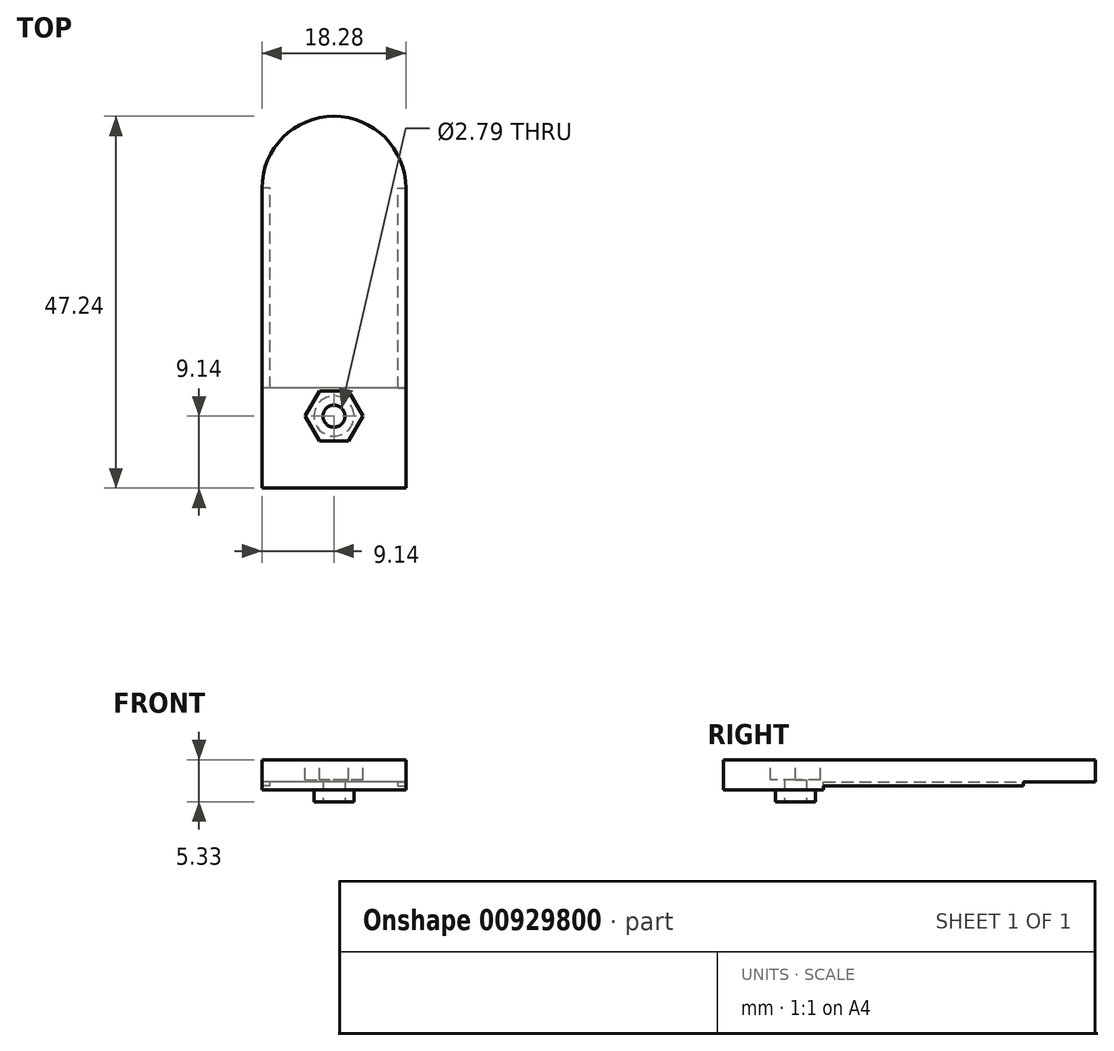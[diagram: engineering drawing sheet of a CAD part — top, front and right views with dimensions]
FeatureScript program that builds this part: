
annotation { "Feature Type Name" : "Feature", "Feature Type Description" : "" }
export const myFeature = defineFeature(function(context is Context, id is Id, definition is map)
    precondition{}
    {
        {
            var Q0;
            Q0=qCreatedBy(makeId("Top.planeOp"),FACE);
            var sketch = newSketch(context, id + "F0", { "sketchPlane" : qUnion([Q0])});
            skCircle(sketch, "E0", {"center": v(0, 0) * mm, "radius": 2.54 * mm});
            skLineSegment(sketch, "E1", {"start": v(0, 0) * mm, "end": v(-8.13, 0) * mm});
            skLineSegment(sketch, "E2", {"start": v(0, 0) * mm, "end": v(8.13, 0) * mm});
            skLineSegment(sketch, "E3", {"start": v(-2.54, 0) * mm, "end": v(-8.13, 0) * mm});
            skLineSegment(sketch, "E4", {"start": v(0, -2.54) * mm, "end": v(0, -9.14) * mm});
            skLineSegment(sketch, "E5", {"start": v(-8.13, 0) * mm, "end": v(-9.14, 0) * mm});
            skLineSegment(sketch, "E6", {"start": v(8.13, 0) * mm, "end": v(9.14, 0) * mm});
            skLineSegment(sketch, "E7", {"start": v(9.14, 0) * mm, "end": v(9.14, -9.14) * mm});
            skLineSegment(sketch, "E8.bottom", {"start": v(9.14, -9.14) * mm, "end": v(-9.14, -9.14) * mm});
            skLineSegment(sketch, "E8.top", {"start": v(9.14, 9.14) * mm, "end": v(-9.14, 9.14) * mm});
            skLineSegment(sketch, "E8.left", {"start": v(9.14, -9.14) * mm, "end": v(9.14, 9.14) * mm});
            skLineSegment(sketch, "E8.right", {"start": v(-9.14, -9.14) * mm, "end": v(-9.14, 9.14) * mm});
            skLineSegment(sketch, "E9", {"start": v(0, 2.54) * mm, "end": v(0, 3.56) * mm});
            skLineSegment(sketch, "E10", {"start": v(-8.13, 0) * mm, "end": v(-8.13, 3.56) * mm});
            skLineSegment(sketch, "E11", {"start": v(-8.13, 3.56) * mm, "end": v(-8.13, 28.96) * mm});
            skLineSegment(sketch, "E12", {"start": v(8.13, 0) * mm, "end": v(8.13, 3.56) * mm});
            skLineSegment(sketch, "E13.bottom", {"start": v(8.13, 3.56) * mm, "end": v(-8.13, 3.56) * mm});
            skLineSegment(sketch, "E13.top", {"start": v(8.13, 28.96) * mm, "end": v(-8.13, 28.96) * mm});
            skLineSegment(sketch, "E13.left", {"start": v(8.13, 3.56) * mm, "end": v(8.13, 28.96) * mm});
            skLineSegment(sketch, "E14", {"start": v(-8.13, 28.96) * mm, "end": v(-9.14, 28.96) * mm});
            skLineSegment(sketch, "E15", {"start": v(8.13, 28.96) * mm, "end": v(9.14, 28.96) * mm});
            skLineSegment(sketch, "E16", {"start": v(-9.14, 28.96) * mm, "end": v(-9.14, 9.14) * mm});
            skLineSegment(sketch, "E17", {"start": v(9.14, 28.96) * mm, "end": v(9.14, 9.14) * mm});
            skCircle(sketch, "E18", {"center": v(0, 28.96) * mm, "radius": 2.54 * mm});
            skCircle(sketch, "E19", {"center": v(0, 28.96) * mm, "radius": 9.14 * mm});
            skLineSegment(sketch, "E20", {"start": v(-8.13, 3.56) * mm, "end": v(-9.14, 3.56) * mm});
            skLineSegment(sketch, "E21", {"start": v(8.13, 3.56) * mm, "end": v(9.14, 3.56) * mm});
            skSolve(sketch);
        }
        {
            var Q0;
            {var subQ1=sQuery(id+"F0.wireOp",EDGE,"E14");Q0=makeQuery(id+"F0.imprint","IMPRINT",FACE,{"disambiguationData":[TD([[makeQuery(id+"F0.imprint","IMPRINT",EDGE,{"derivedFrom":subQ1}),-1.0]])]});}
            var Q1;
            {var subQ1=sQuery(id+"F0.wireOp",EDGE,"E13.top");var subQ5=sQuery(id+"F0.wireOp",EDGE,"E18");var subQ7=makeQuery(id+"F0.imprint","INTERSECT",VERTEX,{"disambiguationData":[OD(0.0)],"derivedFrom":[subQ1,subQ5]});Q1=makeQuery(id+"F0.imprint","IMPRINT",FACE,{"disambiguationData":[TD([[makeQuery(id+"F0.imprint","IMPRINT",EDGE,{"disambiguationData":[TD([[subQ7,-1.0]])],"derivedFrom":subQ5}),-1.0]])]});}
            var Q2;
            {var subQ3=sQuery(id+"F0.wireOp",EDGE,"E17");Q2=makeQuery(id+"F0.imprint","IMPRINT",FACE,{"disambiguationData":[TD([[makeQuery(id+"F0.imprint","IMPRINT",EDGE,{"derivedFrom":subQ3}),-1.0]])]});}
            var Q3;
            {var subQ0=sQuery(id+"F0.wireOp",EDGE,"E15");Q3=makeQuery(id+"F0.imprint","IMPRINT",FACE,{"disambiguationData":[TD([[makeQuery(id+"F0.imprint","IMPRINT",EDGE,{"derivedFrom":subQ0}),-1.0]])]});}
            var Q4;
            {var subQ0=sQuery(id+"F0.wireOp",EDGE,"E18");var subQ1=sQuery(id+"F0.wireOp",EDGE,"E13.top");var subQ2=makeQuery(id+"F0.imprint","INTERSECT",VERTEX,{"disambiguationData":[OD(0.0)],"derivedFrom":[subQ1,subQ0]});Q4=makeQuery(id+"F0.imprint","IMPRINT",FACE,{"disambiguationData":[TD([[makeQuery(id+"F0.imprint","IMPRINT",EDGE,{"disambiguationData":[TD([[subQ2,1.0]])],"derivedFrom":subQ1}),1.0]])]});}
            var Q5;
            {var subQ0=sQuery(id+"F0.wireOp",EDGE,"E18");var subQ1=sQuery(id+"F0.wireOp",EDGE,"E13.top");var subQ2=makeQuery(id+"F0.imprint","INTERSECT",VERTEX,{"disambiguationData":[OD(0.0)],"derivedFrom":[subQ1,subQ0]});Q5=makeQuery(id+"F0.imprint","IMPRINT",FACE,{"disambiguationData":[TD([[makeQuery(id+"F0.imprint","IMPRINT",EDGE,{"disambiguationData":[TD([[subQ2,1.0]])],"derivedFrom":subQ1}),-1.0]])]});}
            var Q6;
            {var subQ0=sQuery(id+"F0.wireOp",EDGE,"E14");Q6=makeQuery(id+"F0.imprint","IMPRINT",FACE,{"disambiguationData":[TD([[makeQuery(id+"F0.imprint","IMPRINT",EDGE,{"derivedFrom":subQ0}),1.0]])]});}
            var Q7;
            {var subQ0=sQuery(id+"F0.wireOp",EDGE,"E16");Q7=makeQuery(id+"F0.imprint","IMPRINT",FACE,{"disambiguationData":[TD([[makeQuery(id+"F0.imprint","IMPRINT",EDGE,{"derivedFrom":subQ0}),1.0]])]});}
            var Q8;
            {var subQ0=sQuery(id+"F0.wireOp",EDGE,"E13.left");var subQ1=sQuery(id+"F0.wireOp",EDGE,"E8.top");var subQ2=makeQuery(id+"F0.imprint","INTERSECT",VERTEX,{"derivedFrom":[subQ1,subQ0]});Q8=makeQuery(id+"F0.imprint","IMPRINT",FACE,{"disambiguationData":[TD([[makeQuery(id+"F0.imprint","IMPRINT",EDGE,{"disambiguationData":[TD([[subQ2,-1.0]])],"derivedFrom":subQ1}),-1.0]])]});}
            var Q9;
            {var subQ2=sQuery(id+"F0.wireOp",EDGE,"E13.left");var subQ6=sQuery(id+"F0.wireOp",EDGE,"E8.top");var subQ8=makeQuery(id+"F0.imprint","INTERSECT",VERTEX,{"derivedFrom":[subQ6,subQ2]});Q9=makeQuery(id+"F0.imprint","IMPRINT",FACE,{"disambiguationData":[TD([[makeQuery(id+"F0.imprint","IMPRINT",EDGE,{"disambiguationData":[TD([[subQ8,-1.0]])],"derivedFrom":subQ6}),1.0]])]});}
            var Q10;
            {var subQ4=sQuery(id+"F0.wireOp",EDGE,"E9");Q10=makeQuery(id+"F0.imprint","IMPRINT",FACE,{"disambiguationData":[TD([[makeQuery(id+"F0.imprint","IMPRINT",EDGE,{"derivedFrom":subQ4}),1.0]])]});}
            var Q11;
            {var subQ0=sQuery(id+"F0.wireOp",EDGE,"E4");Q11=makeQuery(id+"F0.imprint","IMPRINT",FACE,{"disambiguationData":[TD([[makeQuery(id+"F0.imprint","IMPRINT",EDGE,{"derivedFrom":subQ0}),-1.0]])]});}
            var Q12;
            {var subQ0=sQuery(id+"F0.wireOp",EDGE,"E5");Q12=makeQuery(id+"F0.imprint","IMPRINT",FACE,{"disambiguationData":[TD([[makeQuery(id+"F0.imprint","IMPRINT",EDGE,{"derivedFrom":subQ0}),-1.0]])]});}
            var Q13;
            {var subQ1=sQuery(id+"F0.wireOp",EDGE,"E9");Q13=makeQuery(id+"F0.imprint","IMPRINT",FACE,{"disambiguationData":[TD([[makeQuery(id+"F0.imprint","IMPRINT",EDGE,{"derivedFrom":subQ1}),-1.0]])]});}
            var Q14;
            {var subQ0=sQuery(id+"F0.wireOp",EDGE,"E6");Q14=makeQuery(id+"F0.imprint","IMPRINT",FACE,{"disambiguationData":[TD([[makeQuery(id+"F0.imprint","IMPRINT",EDGE,{"derivedFrom":subQ0}),1.0]])]});}
            var Q15;
            {var subQ4=sQuery(id+"F0.wireOp",EDGE,"E4");Q15=makeQuery(id+"F0.imprint","IMPRINT",FACE,{"disambiguationData":[TD([[makeQuery(id+"F0.imprint","IMPRINT",EDGE,{"derivedFrom":subQ4}),1.0]])]});}
            var Q16;
            {var subQ0=sQuery(id+"F0.wireOp",EDGE,"E1");var subQ1=sQuery(id+"F0.wireOp",EDGE,"E0");var subQ2=makeQuery(id+"F0.imprint","INTERSECT",VERTEX,{"derivedFrom":[subQ1,subQ0]});Q16=makeQuery(id+"F0.imprint","IMPRINT",FACE,{"disambiguationData":[TD([[makeQuery(id+"F0.imprint","IMPRINT",EDGE,{"disambiguationData":[TD([[subQ2,-1.0]])],"derivedFrom":subQ1}),1.0]])]});}
            var Q17;
            {var subQ0=sQuery(id+"F0.wireOp",EDGE,"E2");var subQ1=sQuery(id+"F0.wireOp",EDGE,"E0");var subQ2=makeQuery(id+"F0.imprint","INTERSECT",VERTEX,{"derivedFrom":[subQ1,subQ0]});Q17=makeQuery(id+"F0.imprint","IMPRINT",FACE,{"disambiguationData":[TD([[makeQuery(id+"F0.imprint","IMPRINT",EDGE,{"disambiguationData":[TD([[subQ2,-1.0]])],"derivedFrom":subQ1}),1.0]])]});}
            var Q18;
            {var subQ5=sQuery(id+"F0.wireOp",EDGE,"E20");Q18=makeQuery(id+"F0.imprint","IMPRINT",FACE,{"disambiguationData":[TD([[makeQuery(id+"F0.imprint","IMPRINT",EDGE,{"derivedFrom":subQ5}),-1.0]])]});}
            var Q19;
            {var subQ5=sQuery(id+"F0.wireOp",EDGE,"E21");Q19=makeQuery(id+"F0.imprint","IMPRINT",FACE,{"disambiguationData":[TD([[makeQuery(id+"F0.imprint","IMPRINT",EDGE,{"derivedFrom":subQ5}),1.0]])]});}
            extrude(context, id + "F1", {"entities" : qUnion([Q0, Q1, Q2, Q3, Q4, Q5, Q6, Q7, Q8, Q9, Q10, Q11, Q12, Q13, Q14, Q15, Q16, Q17, Q18, Q19]), "depth" : 2.8 * mm, "offsetDistance" : 25.4 * mm});
        }
        {
            var Q0;
            {var subQ0=sQuery(id+"F0.wireOp",EDGE,"E14");Q0=makeQuery(id+"F0.imprint","IMPRINT",FACE,{"disambiguationData":[TD([[makeQuery(id+"F0.imprint","IMPRINT",EDGE,{"derivedFrom":subQ0}),1.0]])]});}
            var Q1;
            {var subQ0=sQuery(id+"F0.wireOp",EDGE,"E16");Q1=makeQuery(id+"F0.imprint","IMPRINT",FACE,{"disambiguationData":[TD([[makeQuery(id+"F0.imprint","IMPRINT",EDGE,{"derivedFrom":subQ0}),1.0]])]});}
            var Q2;
            {var subQ3=sQuery(id+"F0.wireOp",EDGE,"E17");Q2=makeQuery(id+"F0.imprint","IMPRINT",FACE,{"disambiguationData":[TD([[makeQuery(id+"F0.imprint","IMPRINT",EDGE,{"derivedFrom":subQ3}),-1.0]])]});}
            var Q3;
            {var subQ0=sQuery(id+"F0.wireOp",EDGE,"E15");Q3=makeQuery(id+"F0.imprint","IMPRINT",FACE,{"disambiguationData":[TD([[makeQuery(id+"F0.imprint","IMPRINT",EDGE,{"derivedFrom":subQ0}),-1.0]])]});}
            var Q4;
            {var subQ5=sQuery(id+"F0.wireOp",EDGE,"E20");Q4=makeQuery(id+"F0.imprint","IMPRINT",FACE,{"disambiguationData":[TD([[makeQuery(id+"F0.imprint","IMPRINT",EDGE,{"derivedFrom":subQ5}),-1.0]])]});}
            var Q5;
            {var subQ5=sQuery(id+"F0.wireOp",EDGE,"E21");Q5=makeQuery(id+"F0.imprint","IMPRINT",FACE,{"disambiguationData":[TD([[makeQuery(id+"F0.imprint","IMPRINT",EDGE,{"derivedFrom":subQ5}),1.0]])]});}
            extrude(context, id + "F2", {"entities" : qUnion([Q0, Q1, Q2, Q3, Q4, Q5]), "operationType" : NewBodyOperationType.ADD, "oppositeDirection" : true, "depth" : 0.5 * mm, "offsetDistance" : 25.4 * mm});
        }
        {
            var Q0;
            {var subQ0=sQuery(id+"F0.wireOp",EDGE,"E4");Q0=makeQuery(id+"F0.imprint","IMPRINT",FACE,{"disambiguationData":[TD([[makeQuery(id+"F0.imprint","IMPRINT",EDGE,{"derivedFrom":subQ0}),-1.0]])]});}
            var Q1;
            {var subQ4=sQuery(id+"F0.wireOp",EDGE,"E9");Q1=makeQuery(id+"F0.imprint","IMPRINT",FACE,{"disambiguationData":[TD([[makeQuery(id+"F0.imprint","IMPRINT",EDGE,{"derivedFrom":subQ4}),1.0]])]});}
            var Q2;
            {var subQ0=sQuery(id+"F0.wireOp",EDGE,"E1");var subQ1=sQuery(id+"F0.wireOp",EDGE,"E0");var subQ2=makeQuery(id+"F0.imprint","INTERSECT",VERTEX,{"derivedFrom":[subQ1,subQ0]});Q2=makeQuery(id+"F0.imprint","IMPRINT",FACE,{"disambiguationData":[TD([[makeQuery(id+"F0.imprint","IMPRINT",EDGE,{"disambiguationData":[TD([[subQ2,-1.0]])],"derivedFrom":subQ1}),1.0]])]});}
            var Q3;
            {var subQ0=sQuery(id+"F0.wireOp",EDGE,"E2");var subQ1=sQuery(id+"F0.wireOp",EDGE,"E0");var subQ2=makeQuery(id+"F0.imprint","INTERSECT",VERTEX,{"derivedFrom":[subQ1,subQ0]});Q3=makeQuery(id+"F0.imprint","IMPRINT",FACE,{"disambiguationData":[TD([[makeQuery(id+"F0.imprint","IMPRINT",EDGE,{"disambiguationData":[TD([[subQ2,-1.0]])],"derivedFrom":subQ1}),1.0]])]});}
            var Q4;
            {var subQ1=sQuery(id+"F0.wireOp",EDGE,"E9");Q4=makeQuery(id+"F0.imprint","IMPRINT",FACE,{"disambiguationData":[TD([[makeQuery(id+"F0.imprint","IMPRINT",EDGE,{"derivedFrom":subQ1}),-1.0]])]});}
            var Q5;
            {var subQ4=sQuery(id+"F0.wireOp",EDGE,"E4");Q5=makeQuery(id+"F0.imprint","IMPRINT",FACE,{"disambiguationData":[TD([[makeQuery(id+"F0.imprint","IMPRINT",EDGE,{"derivedFrom":subQ4}),1.0]])]});}
            var Q6;
            {var subQ0=sQuery(id+"F0.wireOp",EDGE,"E5");Q6=makeQuery(id+"F0.imprint","IMPRINT",FACE,{"disambiguationData":[TD([[makeQuery(id+"F0.imprint","IMPRINT",EDGE,{"derivedFrom":subQ0}),-1.0]])]});}
            var Q7;
            {var subQ0=sQuery(id+"F0.wireOp",EDGE,"E6");Q7=makeQuery(id+"F0.imprint","IMPRINT",FACE,{"disambiguationData":[TD([[makeQuery(id+"F0.imprint","IMPRINT",EDGE,{"derivedFrom":subQ0}),1.0]])]});}
            extrude(context, id + "F3", {"entities" : qUnion([Q0, Q1, Q2, Q3, Q4, Q5, Q6, Q7]), "operationType" : NewBodyOperationType.ADD, "oppositeDirection" : true, "depth" : 1.02 * mm, "offsetDistance" : 25.4 * mm});
        }
        {
            var Q0;
            Q0=makeQuery(id+"F3.opExtrude","CAP_FACE",FACE,{"disambiguationData":[OSD([sQuery(id+"F0.wireOp",EDGE,"E7"),sQuery(id+"F0.wireOp",EDGE,"E8.bottom"),sQuery(id+"F0.wireOp",EDGE,"E8.left"),sQuery(id+"F0.wireOp",EDGE,"E8.right"),sQuery(id+"F0.wireOp",EDGE,"E13.bottom"),sQuery(id+"F0.wireOp",EDGE,"E20"),sQuery(id+"F0.wireOp",EDGE,"E21")])],"isStart":false});
            var sketch = newSketch(context, id + "F4", { "sketchPlane" : qUnion([Q0])});
            skLineSegment(sketch, "E22", {"start": v(0, 0) * mm, "end": v(2.54, 0) * mm});
            skCircle(sketch, "E23", {"center": v(0, 0) * mm, "radius": 2.54 * mm});
            skSolve(sketch);
        }
        {
            var Q0;
            Q0=makeQuery(id+"F4.imprint","IMPRINT",FACE,{"disambiguationData":[TD([[makeQuery(id+"F4.imprint","IMPRINT",EDGE,{"derivedFrom":sQuery(id+"F4.wireOp",EDGE,"E23")}),1.0]])]});
            extrude(context, id + "F5", {"entities" : qUnion([Q0]), "operationType" : NewBodyOperationType.ADD, "depth" : 1.52 * mm, "offsetDistance" : 25.4 * mm});
        }
        {
            var Q0;
            Q0=makeQuery(id+"F5.opExtrude","CAP_FACE",FACE,{"disambiguationData":[OSD([sQuery(id+"F4.wireOp",EDGE,"E23")])],"isStart":false});
            var sketch = newSketch(context, id + "F6", { "sketchPlane" : qUnion([Q0])});
            skCircle(sketch, "E24", {"center": v(0, 0) * mm, "radius": 1.4 * mm});
            skSolve(sketch);
        }
        {
            var Q0;
            Q0=makeQuery(id+"F6.imprint","IMPRINT",FACE,{"disambiguationData":[TD([[makeQuery(id+"F6.imprint","IMPRINT",EDGE,{"derivedFrom":sQuery(id+"F6.wireOp",EDGE,"E24")}),1.0]])]});
            var Q1;
            Q1=makeQuery(id+"F1.opExtrude","SWEPT_BODY",BODY,{"disambiguationData":[OSD([sQuery(id+"F0.wireOp",EDGE,"E7"),sQuery(id+"F0.wireOp",EDGE,"E8.bottom"),sQuery(id+"F0.wireOp",EDGE,"E8.left"),sQuery(id+"F0.wireOp",EDGE,"E8.right"),sQuery(id+"F0.wireOp",EDGE,"E16"),sQuery(id+"F0.wireOp",EDGE,"E17"),sQuery(id+"F0.wireOp",EDGE,"E19")])]});
            extrude(context, id + "F7", {"entities" : qUnion([Q0]), "operationType" : NewBodyOperationType.REMOVE, "endBound" : BoundingType.UP_TO_BODY, "oppositeDirection" : true, "depth" : 25.4 * mm, "endBoundEntityBody" : qUnion([Q1]), "offsetDistance" : 25.4 * mm});
        }
        {
            var Q0;
            Q0=makeQuery(id+"F1.opExtrude","CAP_FACE",FACE,{"disambiguationData":[OSD([sQuery(id+"F0.wireOp",EDGE,"E7"),sQuery(id+"F0.wireOp",EDGE,"E8.bottom"),sQuery(id+"F0.wireOp",EDGE,"E8.left"),sQuery(id+"F0.wireOp",EDGE,"E8.right"),sQuery(id+"F0.wireOp",EDGE,"E16"),sQuery(id+"F0.wireOp",EDGE,"E17"),sQuery(id+"F0.wireOp",EDGE,"E19")])],"isStart":false});
            var sketch = newSketch(context, id + "F8", { "sketchPlane" : qUnion([Q0])});
            skLineSegment(sketch, "E25", {"start": v(0, 0) * mm, "end": v(0, -3.18) * mm});
            skLineSegment(sketch, "E26", {"start": v(0, 0) * mm, "end": v(3.18, 0) * mm});
            skCircle(sketch, "E27.cCircle", {"center": v(0, 0) * mm, "radius": 3.18 * mm, "construction": true});
            skLineSegment(sketch, "E27.0", {"start": v(1.83, -3.18) * mm, "end": v(-1.83, -3.18) * mm});
            skLineSegment(sketch, "E27.1", {"start": v(-1.83, -3.18) * mm, "end": v(-3.67, 0) * mm});
            skLineSegment(sketch, "E27.2", {"start": v(-3.67, 0) * mm, "end": v(-1.83, 3.17) * mm});
            skLineSegment(sketch, "E27.3", {"start": v(-1.83, 3.17) * mm, "end": v(1.83, 3.18) * mm});
            skLineSegment(sketch, "E27.4", {"start": v(1.83, 3.18) * mm, "end": v(3.67, 0) * mm});
            skLineSegment(sketch, "E27.5", {"start": v(3.67, 0) * mm, "end": v(1.83, -3.17) * mm});
            skPoint(sketch, "E27.0.midPoint", {"position": v(0, -3.18) * mm});
            skSolve(sketch);
        }
        {
            var Q0;
            {var subQ0=sQuery(id+"F8.wireOp",EDGE,"E27.1");Q0=makeQuery(id+"F8.imprint","IMPRINT",FACE,{"disambiguationData":[TD([[makeQuery(id+"F8.imprint","IMPRINT",EDGE,{"derivedFrom":subQ0}),-1.0]])]});}
            extrude(context, id + "F9", {"entities" : qUnion([Q0]), "operationType" : NewBodyOperationType.REMOVE, "oppositeDirection" : true, "depth" : 2.54 * mm, "offsetDistance" : 25.4 * mm});
        }
    });
